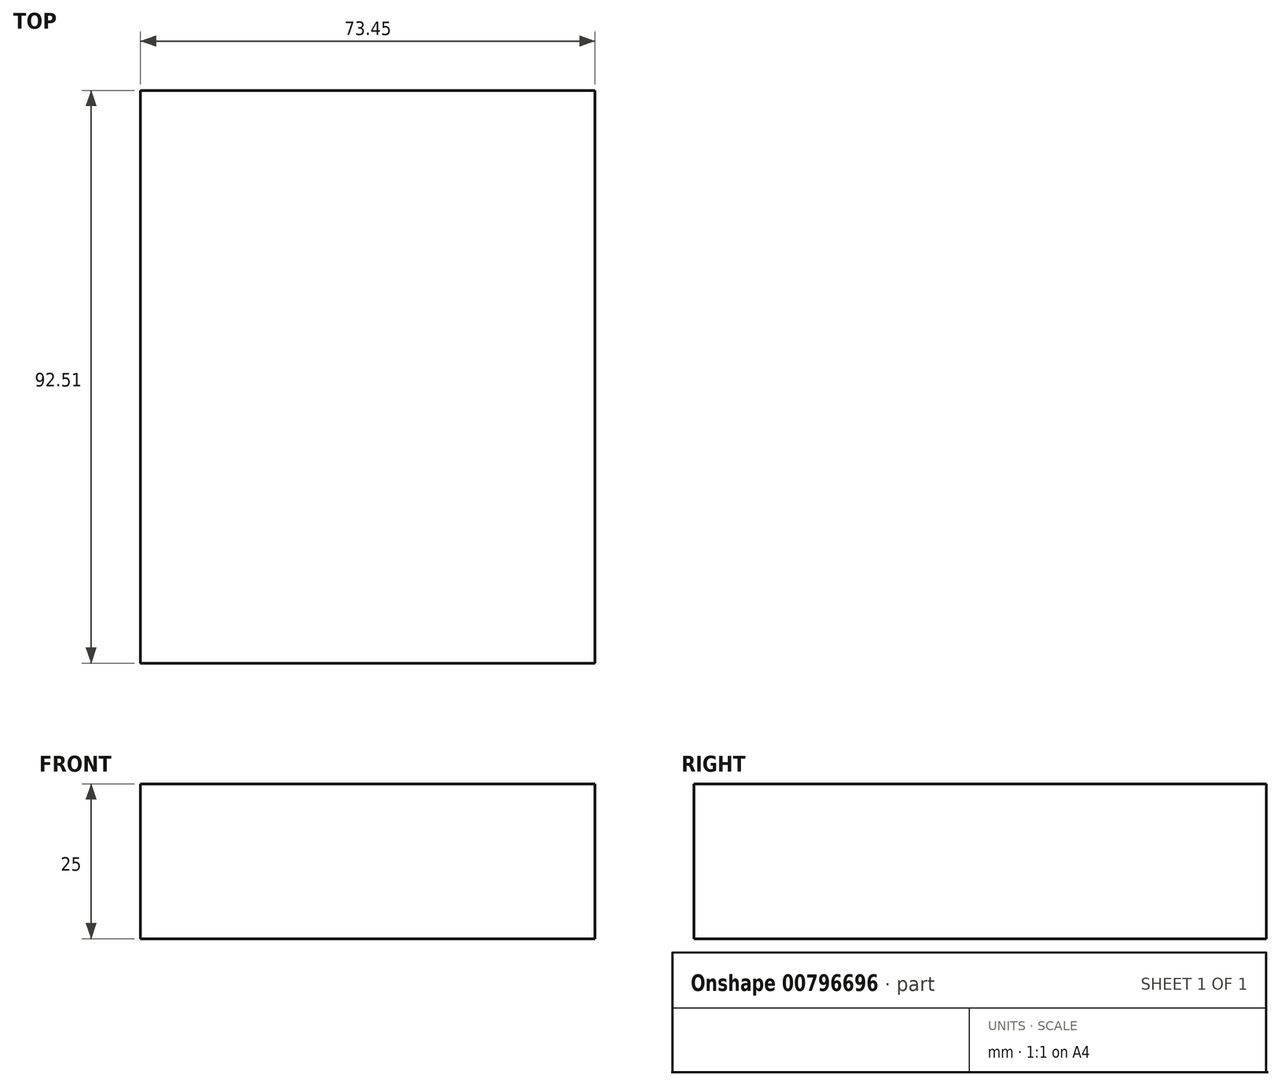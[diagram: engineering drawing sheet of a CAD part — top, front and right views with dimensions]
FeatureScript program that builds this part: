
annotation { "Feature Type Name" : "Feature", "Feature Type Description" : "" }
export const myFeature = defineFeature(function(context is Context, id is Id, definition is map)
    precondition{}
    {
        {
            var Q0;
            Q0=qCreatedBy(makeId("Top.planeOp"),FACE);
            var sketch = newSketch(context, id + "F0", { "sketchPlane" : qUnion([Q0])});
            skLineSegment(sketch, "E0.bottom", {"start": v(0, 10.73) * mm, "end": v(73.45, 10.73) * mm});
            skLineSegment(sketch, "E0.top", {"start": v(0, -81.78) * mm, "end": v(73.45, -81.78) * mm});
            skLineSegment(sketch, "E0.left", {"start": v(0, 10.73) * mm, "end": v(0, -81.78) * mm});
            skLineSegment(sketch, "E0.right", {"start": v(73.45, 10.73) * mm, "end": v(73.45, -81.78) * mm});
            skSolve(sketch);
        }
        {
            var Q0;
            Q0 = qSketchRegion(id + "F0", true);
            extrude(context, id + "F1", {"entities" : qUnion([Q0]), "depth" : 25 * mm, "offsetDistance" : 25 * mm});
        }
    });
